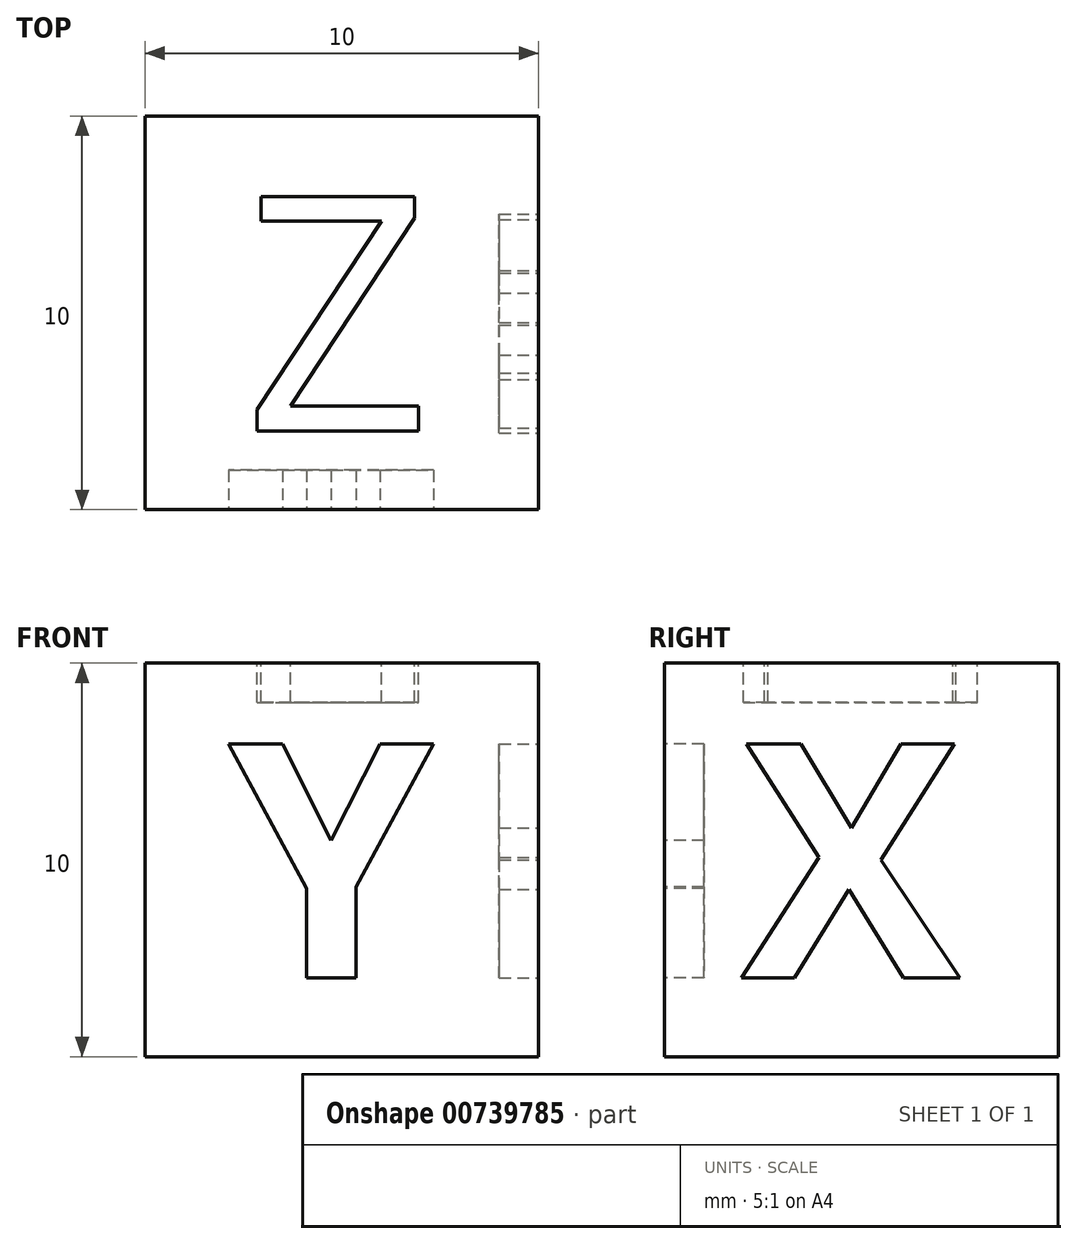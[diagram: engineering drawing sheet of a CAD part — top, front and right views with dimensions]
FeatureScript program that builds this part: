
annotation { "Feature Type Name" : "Feature", "Feature Type Description" : "" }
export const myFeature = defineFeature(function(context is Context, id is Id, definition is map)
    precondition{}
    {
        {
            assignVariable(context, id + "F0", {"name" : "Dimension", "anyValue" : 10});
        }
        {
            var Q0;
            Q0=qCreatedBy(makeId("Top.planeOp"),FACE);
            var sketch = newSketch(context, id + "F1", { "sketchPlane" : qUnion([Q0])});
            skLineSegment(sketch, "E0.bottom", {"start": v(5, -5) * mm, "end": v(-5, -5) * mm});
            skLineSegment(sketch, "E0.top", {"start": v(5, 5) * mm, "end": v(-5, 5) * mm});
            skLineSegment(sketch, "E0.left", {"start": v(5, -5) * mm, "end": v(5, 5) * mm});
            skLineSegment(sketch, "E0.right", {"start": v(-5, -5) * mm, "end": v(-5, 5) * mm});
            skPoint(sketch, "E0.middle", {"position": v(0, 0) * mm});
            skSolve(sketch);
        }
        {
            var Q0;
            Q0 = qSketchRegion(id + "F1", true);
            extrude(context, id + "F2", {"entities" : qUnion([Q0]), "depth" : (getVariable(context, 'Dimension')) * mm, "offsetDistance" : 25 * mm});
        }
        {
            var Q0;
            Q0=makeQuery(id+"F2.opExtrude","SWEPT_FACE",FACE,{"disambiguationData":[OSD([sQuery(id+"F1.wireOp",EDGE,"E0.bottom")])]});
            cPlane(context, id + "F3", {"entities" : qUnion([Q0]), "cplaneType" : CPlaneType.OFFSET, "offset" : 0 * mm, "width" : 150 * mm, "height" : 150 * mm});
        }
        {
            var Q0;
            Q0=qCreatedBy(id+"F3.planeOp",FACE);
            var sketch = newSketch(context, id + "F4", { "sketchPlane" : qUnion([Q0])});
            skText(sketch, "E1", { "text": "Y", "fontName": "OpenSans-Bold.ttf"});
            const initialGuessF4  = {"E1": [-0.00287, 0.002, 1, 0, 0.006]};
            skSetInitialGuess(sketch, initialGuessF4);
            skSolve(sketch);
        }
        {
            var Q0;
            Q0 = qSketchRegion(id + "F4", true);
            extrude(context, id + "F5", {"entities" : qUnion([Q0]), "operationType" : NewBodyOperationType.REMOVE, "oppositeDirection" : true, "depth" : 1 * mm, "offsetDistance" : 25 * mm});
        }
        {
            var Q0;
            Q0=makeQuery(id+"F2.opExtrude","SWEPT_FACE",FACE,{"disambiguationData":[OSD([sQuery(id+"F1.wireOp",EDGE,"E0.left")])]});
            cPlane(context, id + "F6", {"entities" : qUnion([Q0]), "cplaneType" : CPlaneType.OFFSET, "offset" : 0 * mm, "width" : 150 * mm, "height" : 150 * mm});
        }
        {
            var Q0;
            Q0=qCreatedBy(id+"F6.planeOp",FACE);
            var sketch = newSketch(context, id + "F7", { "sketchPlane" : qUnion([Q0])});
            skText(sketch, "E2", { "text": "X", "fontName": "OpenSans-Bold.ttf"});
            const initialGuessF7  = {"E2": [-0.00305, 0.002, 1, 0, 0.006]};
            skSetInitialGuess(sketch, initialGuessF7);
            skSolve(sketch);
        }
        {
            var Q0;
            Q0 = qSketchRegion(id + "F7", true);
            extrude(context, id + "F8", {"entities" : qUnion([Q0]), "operationType" : NewBodyOperationType.REMOVE, "oppositeDirection" : true, "depth" : 1 * mm, "offsetDistance" : 25 * mm});
        }
        {
            var Q0;
            Q0=makeQuery(id+"F2.opExtrude","CAP_FACE",FACE,{"disambiguationData":[OSD([sQuery(id+"F1.wireOp",EDGE,"E0.bottom"),sQuery(id+"F1.wireOp",EDGE,"E0.top"),sQuery(id+"F1.wireOp",EDGE,"E0.left"),sQuery(id+"F1.wireOp",EDGE,"E0.right")])],"isStart":false});
            cPlane(context, id + "F9", {"entities" : qUnion([Q0]), "cplaneType" : CPlaneType.OFFSET, "offset" : 0 * mm, "width" : 150 * mm, "height" : 150 * mm});
        }
        {
            var Q0;
            Q0=qCreatedBy(id+"F9.planeOp",FACE);
            var sketch = newSketch(context, id + "F10", { "sketchPlane" : qUnion([Q0])});
            skText(sketch, "E3", { "text": "Z", "fontName": "OpenSans-Regular.ttf"});
            const initialGuessF10  = {"E3": [-0.00248, -0.003, 1, 0, 0.006]};
            skSetInitialGuess(sketch, initialGuessF10);
            skSolve(sketch);
        }
        {
            var Q0;
            Q0 = qSketchRegion(id + "F10", true);
            extrude(context, id + "F11", {"entities" : qUnion([Q0]), "operationType" : NewBodyOperationType.REMOVE, "oppositeDirection" : true, "depth" : 1 * mm, "offsetDistance" : 25 * mm});
        }
    });
